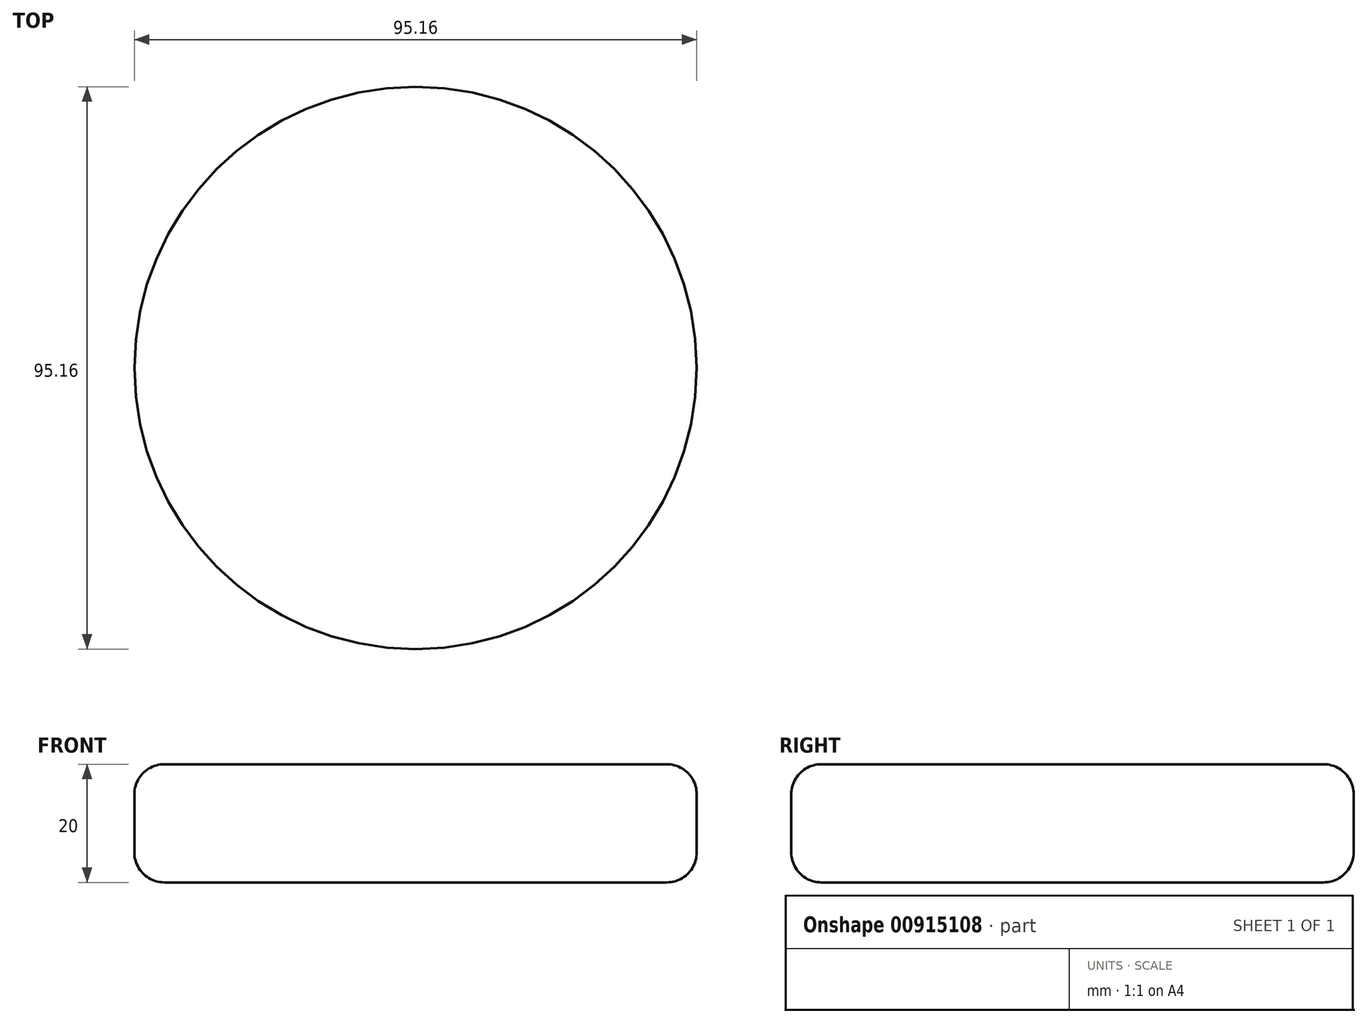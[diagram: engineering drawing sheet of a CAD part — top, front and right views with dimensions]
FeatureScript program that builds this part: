
annotation { "Feature Type Name" : "Feature", "Feature Type Description" : "" }
export const myFeature = defineFeature(function(context is Context, id is Id, definition is map)
    precondition{}
    {
        {
            var Q0;
            Q0=qCreatedBy(makeId("Top.planeOp"),FACE);
            var sketch = newSketch(context, id + "F0", { "sketchPlane" : qUnion([Q0])});
            skCircle(sketch, "E0", {"center": v(0, 0) * mm, "radius": 47.58 * mm});
            skSolve(sketch);
        }
        {
            var Q0;
            Q0 = qSketchRegion(id + "F0", true);
            extrude(context, id + "F1", {"entities" : qUnion([Q0]), "depth" : 20 * mm, "offsetDistance" : 25.4 * mm});
        }
        {
            var Q0;
            Q0=makeQuery(id+"F1.opExtrude","CAP_FACE",FACE,{"disambiguationData":[OSD([sQuery(id+"F0.wireOp",EDGE,"E0")])],"isStart":false});
            var Q1;
            Q1=makeQuery(id+"F1.opExtrude","SWEPT_FACE",FACE,{"disambiguationData":[OSD([sQuery(id+"F0.wireOp",EDGE,"E0")])]});
            fillet(context, id + "F2", {"entities" : qUnion([Q0, Q1]), "radius" : 5.08 * mm, "tangentPropagation" : true, "allowEdgeOverflow" : false});
        }
    });
